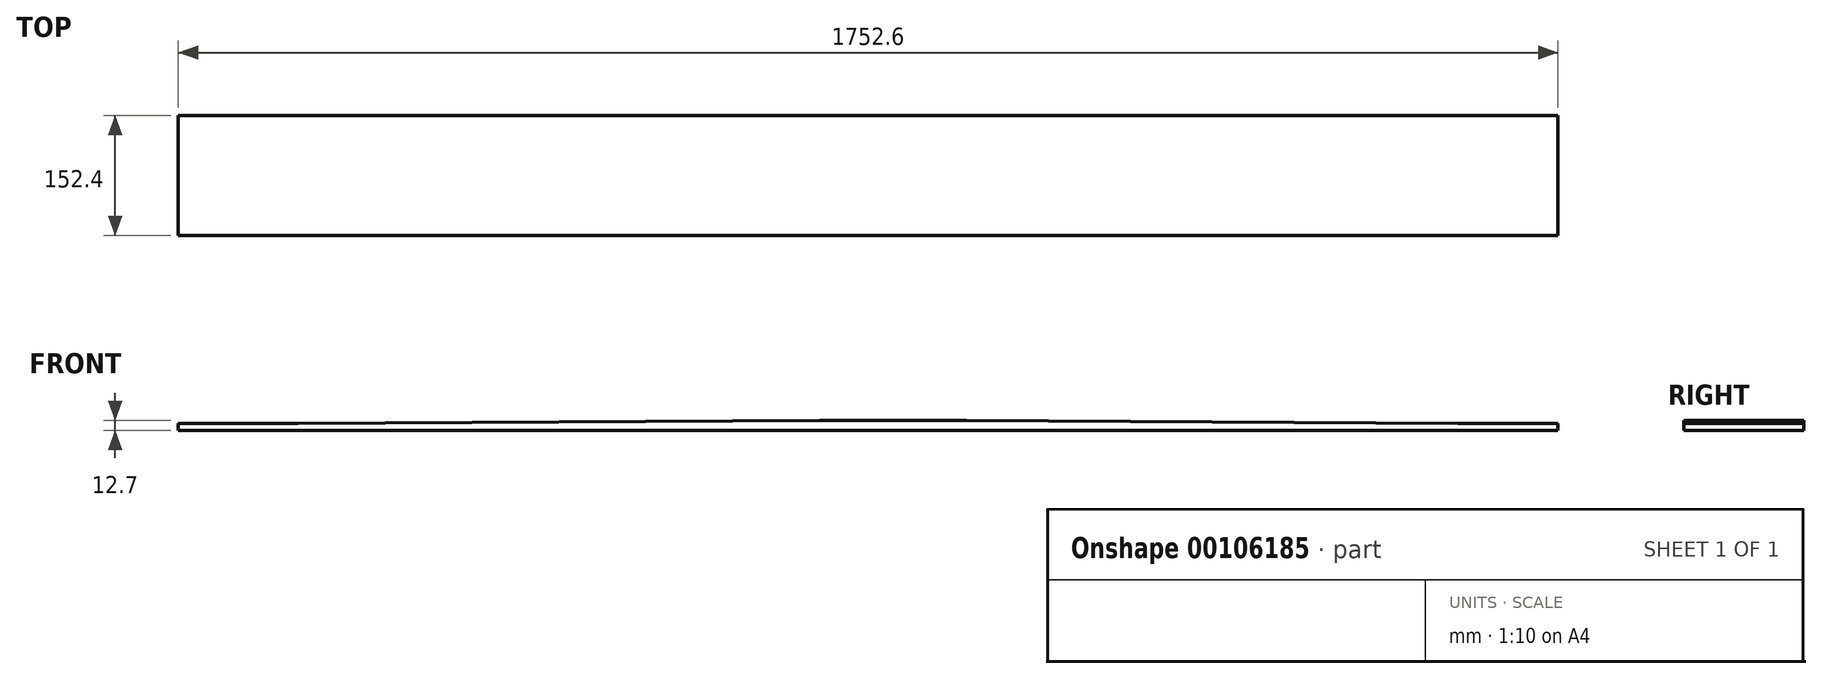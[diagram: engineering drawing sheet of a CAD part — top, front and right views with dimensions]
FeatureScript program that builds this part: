
annotation { "Feature Type Name" : "Feature", "Feature Type Description" : "" }
export const myFeature = defineFeature(function(context is Context, id is Id, definition is map)
    precondition{}
    {
        {
            var Q0;
            Q0=qCreatedBy(makeId("Front.planeOp"),FACE);
            var sketch = newSketch(context, id + "F0", { "sketchPlane" : qUnion([Q0])});
            skLineSegment(sketch, "E0", {"start": v(-884.1, 0) * mm, "end": v(868.5, 0) * mm});
            skLineSegment(sketch, "E1.bottom", {"start": v(-884.1, 0) * mm, "end": v(-731.7, 0) * mm});
            skLineSegment(sketch, "E1.top", {"start": v(-884.1, 8.59) * mm, "end": v(-731.7, 8.59) * mm});
            skLineSegment(sketch, "E1.left", {"start": v(-884.1, 0) * mm, "end": v(-884.1, 8.59) * mm});
            skLineSegment(sketch, "E1.right", {"start": v(-731.7, 0) * mm, "end": v(-731.7, 8.59) * mm});
            skLineSegment(sketch, "E2.bottom", {"start": v(868.5, 0) * mm, "end": v(741.5, 0) * mm});
            skLineSegment(sketch, "E2.top", {"start": v(868.5, 8.59) * mm, "end": v(741.5, 8.59) * mm});
            skLineSegment(sketch, "E2.left", {"start": v(868.5, 0) * mm, "end": v(868.5, 8.59) * mm});
            skLineSegment(sketch, "E2.right", {"start": v(741.5, 0) * mm, "end": v(741.5, 8.59) * mm});
            skLineSegment(sketch, "E3", {"start": v(-69.77, 0) * mm, "end": v(-69.77, 12.7) * mm});
            skLineSegment(sketch, "E4", {"start": v(117.32, 0) * mm, "end": v(117.32, 12.7) * mm});
            skLineSegment(sketch, "E5", {"start": v(-731.7, 8.59) * mm, "end": v(-69.77, 12.7) * mm});
            skLineSegment(sketch, "E6", {"start": v(-69.77, 12.7) * mm, "end": v(117.32, 12.7) * mm});
            skLineSegment(sketch, "E7", {"start": v(741.5, 8.59) * mm, "end": v(117.32, 12.7) * mm});
            skSolve(sketch);
        }
        {
            var Q0;
            Q0 = qSketchRegion(id + "F0", true);
            extrude(context, id + "F1", {"entities" : qUnion([Q0]), "depth" : 152.4 * mm});
        }
    });
